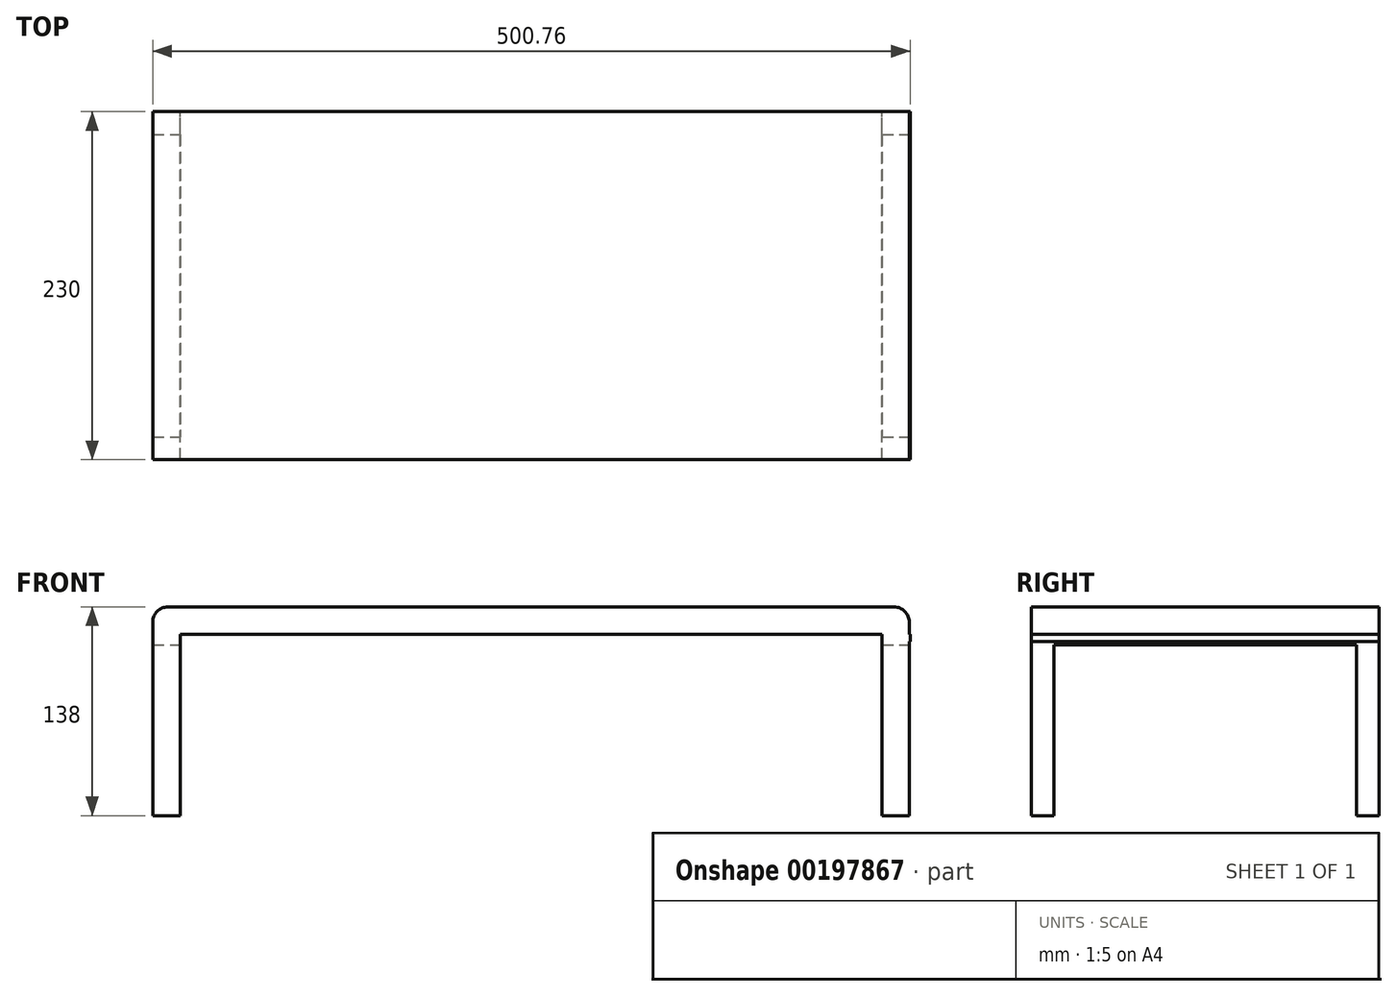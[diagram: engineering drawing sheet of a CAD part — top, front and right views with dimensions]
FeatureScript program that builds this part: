
annotation { "Feature Type Name" : "Feature", "Feature Type Description" : "" }
export const myFeature = defineFeature(function(context is Context, id is Id, definition is map)
    precondition{}
    {
        {
            var Q0;
            Q0=qCreatedBy(makeId("Front.planeOp"),FACE);
            var sketch = newSketch(context, id + "F0", { "sketchPlane" : qUnion([Q0])});
            skLineSegment(sketch, "E0.bottom", {"start": v(-250, 9) * mm, "end": v(250, 9) * mm});
            skLineSegment(sketch, "E0.top", {"start": v(-250, -9) * mm, "end": v(250, -9) * mm});
            skLineSegment(sketch, "E0.left", {"start": v(-250, 9) * mm, "end": v(-250, -9) * mm});
            skLineSegment(sketch, "E0.right", {"start": v(250, 9) * mm, "end": v(250, -9) * mm});
            skPoint(sketch, "E0.middle", {"position": v(0, 0) * mm});
            skLineSegment(sketch, "E1.bottom", {"start": v(-250, -9) * mm, "end": v(-232, -9) * mm});
            skLineSegment(sketch, "E1.top", {"start": v(-250, -129) * mm, "end": v(-232, -129) * mm});
            skLineSegment(sketch, "E1.left", {"start": v(-250, -9) * mm, "end": v(-250, -129) * mm});
            skLineSegment(sketch, "E1.right", {"start": v(-232, -9) * mm, "end": v(-232, -129) * mm});
            skLineSegment(sketch, "E2.bottom", {"start": v(250, -9) * mm, "end": v(232, -9) * mm});
            skLineSegment(sketch, "E2.top", {"start": v(250, -129) * mm, "end": v(232, -129) * mm});
            skLineSegment(sketch, "E2.left", {"start": v(250, -9) * mm, "end": v(250, -129) * mm});
            skLineSegment(sketch, "E2.right", {"start": v(232, -9) * mm, "end": v(232, -129) * mm});
            skSolve(sketch);
        }
        {
            var Q0;
            Q0 = qSketchRegion(id + "F0", true);
            extrude(context, id + "F1", {"entities" : qUnion([Q0]), "endBound" : BoundingType.SYMMETRIC, "depth" : 230 * mm});
        }
        {
            var Q0;
            {var subQ0=sQuery(id+"F0.wireOp",EDGE,"E0.left");var subQ1=sQuery(id+"F0.wireOp",EDGE,"E0.bottom");Q0=makeQuery(id+"FSnjSYWFuBKB38g_0.boolean.opBoolean","MERGE",EDGE,{"derivedFrom":[makeQuery(id+"F1.opExtrude","SWEPT_EDGE",EDGE,{"disambiguationData":[OSD([subQ1,subQ0])]}),makeQuery(id+"FSnjSYWFuBKB38g_0.opExtrude","SWEPT_EDGE",EDGE,{"disambiguationData":[OSD([subQ1,subQ0])]})]});}
            var Q1;
            {var subQ0=sQuery(id+"F0.wireOp",EDGE,"E0.right");var subQ1=sQuery(id+"F0.wireOp",EDGE,"E0.bottom");Q1=makeQuery(id+"FSnjSYWFuBKB38g_0.boolean.opBoolean","MERGE",EDGE,{"derivedFrom":[makeQuery(id+"F1.opExtrude","SWEPT_EDGE",EDGE,{"disambiguationData":[OSD([subQ1,subQ0])]}),makeQuery(id+"FSnjSYWFuBKB38g_0.opExtrude","SWEPT_EDGE",EDGE,{"disambiguationData":[OSD([subQ1,subQ0])]})]});}
            fillet(context, id + "F2", {"entities" : qUnion([Q0, Q1]), "radius" : 10 * mm, "tangentPropagation" : true, "allowEdgeOverflow" : false});
        }
        {
            var Q0;
            Q0=makeQuery(id+"F1.opExtrude","SWEPT_FACE",FACE,{"disambiguationData":[OSD([sQuery(id+"F0.wireOp",EDGE,"E0.right"),sQuery(id+"F0.wireOp",EDGE,"E2.left")])]});
            var sketch = newSketch(context, id + "F3", { "sketchPlane" : qUnion([Q0])});
            skLineSegment(sketch, "E3.bottom", {"start": v(100, -129) * mm, "end": v(-100, -129) * mm});
            skLineSegment(sketch, "E3.top", {"start": v(100, -16) * mm, "end": v(-100, -16) * mm});
            skLineSegment(sketch, "E3.left", {"start": v(100, -129) * mm, "end": v(100, -16) * mm});
            skLineSegment(sketch, "E3.right", {"start": v(-100, -129) * mm, "end": v(-100, -16) * mm});
            skPoint(sketch, "E3.middle", {"position": v(0, -72.5) * mm});
            skSolve(sketch);
        }
        {
            var Q0;
            Q0 = qSketchRegion(id + "F3", true);
            extrude(context, id + "F4", {"entities" : qUnion([Q0]), "operationType" : NewBodyOperationType.REMOVE, "endBound" : BoundingType.THROUGH_ALL, "oppositeDirection" : true, "depth" : 25 * mm});
        }
        {
            var Q0;
            Q0=makeQuery(id+"F1.opExtrude","SWEPT_FACE",FACE,{"disambiguationData":[OSD([sQuery(id+"F0.wireOp",EDGE,"E0.top")])]});
            var sketch = newSketch(context, id + "F5", { "sketchPlane" : qUnion([Q0])});
            skLineSegment(sketch, "E4.bottom", {"start": v(-250.08, 114.76) * mm, "end": v(-232, 114.76) * mm});
            skLineSegment(sketch, "E4.top", {"start": v(-250.08, -115) * mm, "end": v(-232, -115) * mm});
            skLineSegment(sketch, "E4.left", {"start": v(-250.08, 114.76) * mm, "end": v(-250.08, -115) * mm});
            skLineSegment(sketch, "E4.right", {"start": v(-232, 114.76) * mm, "end": v(-232, -115) * mm});
            skLineSegment(sketch, "E5.bottom", {"start": v(232, 115) * mm, "end": v(250.68, 115) * mm});
            skLineSegment(sketch, "E5.top", {"start": v(232, -115) * mm, "end": v(250.68, -115) * mm});
            skLineSegment(sketch, "E5.left", {"start": v(232, 115) * mm, "end": v(232, -115) * mm});
            skLineSegment(sketch, "E5.right", {"start": v(250.68, 115) * mm, "end": v(250.68, -115) * mm});
            skSolve(sketch);
        }
        {
            var Q0;
            Q0 = qSketchRegion(id + "F5", true);
            extrude(context, id + "F6", {"entities" : qUnion([Q0]), "operationType" : NewBodyOperationType.ADD, "depth" : 5 * mm});
        }
    });
